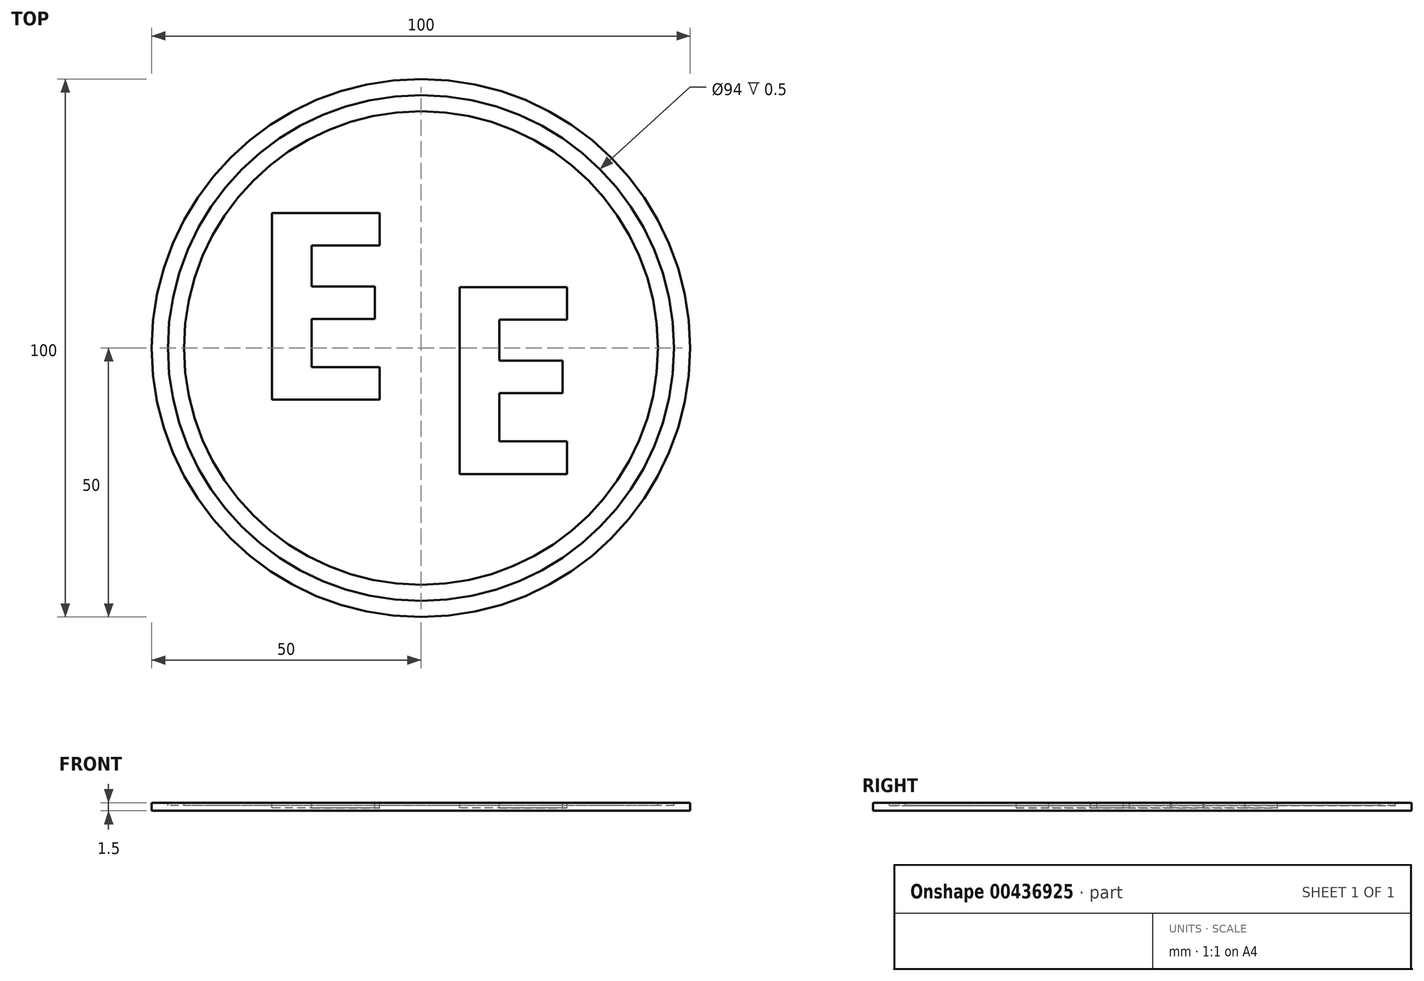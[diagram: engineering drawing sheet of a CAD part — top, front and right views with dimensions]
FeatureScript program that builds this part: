
annotation { "Feature Type Name" : "Feature", "Feature Type Description" : "" }
export const myFeature = defineFeature(function(context is Context, id is Id, definition is map)
    precondition{}
    {
        {
            var Q0;
            Q0=qCreatedBy(makeId("Top.planeOp"),FACE);
            var sketch = newSketch(context, id + "F0", { "sketchPlane" : qUnion([Q0])});
            skCircle(sketch, "E0", {"center": v(0, 0) * mm, "radius": 50 * mm});
            skSolve(sketch);
        }
        {
            var Q0;
            Q0=makeQuery(id+"F0.imprint","IMPRINT",FACE,{"disambiguationData":[TD([[makeQuery(id+"F0.imprint","IMPRINT",EDGE,{"derivedFrom":sQuery(id+"F0.wireOp",EDGE,"E0")}),1.0]])]});
            extrude(context, id + "F1", {"entities" : qUnion([Q0]), "depth" : 1.5 * mm});
        }
        {
            var Q0;
            Q0=makeQuery(id+"F1.opExtrude","CAP_FACE",FACE,{"disambiguationData":[OSD([sQuery(id+"F0.wireOp",EDGE,"E0")])],"isStart":false});
            var sketch = newSketch(context, id + "F2", { "sketchPlane" : qUnion([Q0])});
            skCircle(sketch, "E1.0", {"center": v(0, 0) * mm, "radius": 50 * mm, "construction": true});
            skCircle(sketch, "E2.0", {"center": v(0, 0) * mm, "radius": 47 * mm});
            skCircle(sketch, "E3.0", {"center": v(0, 0) * mm, "radius": 44 * mm});
            skSolve(sketch);
        }
        {
            var Q0;
            Q0 = qSketchRegion(id + "F2", true);
            extrude(context, id + "F3", {"entities" : qUnion([Q0]), "operationType" : NewBodyOperationType.REMOVE, "oppositeDirection" : true, "depth" : .5 * mm});
        }
        {
            var Q0;
            Q0=makeQuery(id+"F3.boolean.opBoolean","SPLIT",FACE,{"disambiguationData":[TD([makeQuery(id+"F3.opExtrude","SWEPT_FACE",FACE,{"disambiguationData":[OSD([sQuery(id+"F2.wireOp",EDGE,"E3.0")])]})])],"derivedFrom":makeQuery(id+"F1.opExtrude","CAP_FACE",FACE,{"disambiguationData":[OSD([sQuery(id+"F0.wireOp",EDGE,"E0")])],"isStart":false})});
            var sketch = newSketch(context, id + "F4", { "sketchPlane" : qUnion([Q0])});
            skText(sketch, "E4", { "text": "E", "fontName": "OpenSans-Bold.ttf"});
            const initialGuessF4  = {"E4": [-0.03202, -0.0096, 1, 0, 0.035]};
            skSetInitialGuess(sketch, initialGuessF4);
            skSolve(sketch);
        }
        {
            var Q0;
            Q0 = qSketchRegion(id + "F4", true);
            extrude(context, id + "F5", {"entities" : qUnion([Q0]), "operationType" : NewBodyOperationType.REMOVE, "oppositeDirection" : true, "depth" : 1 * mm});
        }
        {
            var Q0;
            Q0=makeQuery(id+"F3.boolean.opBoolean","SPLIT",FACE,{"disambiguationData":[TD([makeQuery(id+"F3.opExtrude","SWEPT_FACE",FACE,{"disambiguationData":[OSD([sQuery(id+"F2.wireOp",EDGE,"E3.0")])]})])],"derivedFrom":makeQuery(id+"F1.opExtrude","CAP_FACE",FACE,{"disambiguationData":[OSD([sQuery(id+"F0.wireOp",EDGE,"E0")])],"isStart":false})});
            var sketch = newSketch(context, id + "F6", { "sketchPlane" : qUnion([Q0])});
            skText(sketch, "E5", { "text": "E", "fontName": "OpenSans-Bold.ttf"});
            const initialGuessF6  = {"E5": [0.0028, -0.02343, 1, 0, 0.035]};
            skSetInitialGuess(sketch, initialGuessF6);
            skSolve(sketch);
        }
        {
            var Q0;
            Q0=makeQuery(id+"F6.imprint","IMPRINT",FACE,{"disambiguationData":[TD([[makeQuery(id+"F6.imprint","IMPRINT",EDGE,{"derivedFrom":sQuery(id+"F6.wireOp",EDGE,"E5.sketch_text.stroke-0")}),-1.0]])]});
            extrude(context, id + "F7", {"entities" : qUnion([Q0]), "operationType" : NewBodyOperationType.REMOVE, "oppositeDirection" : true, "depth" : 1 * mm});
        }
    });
